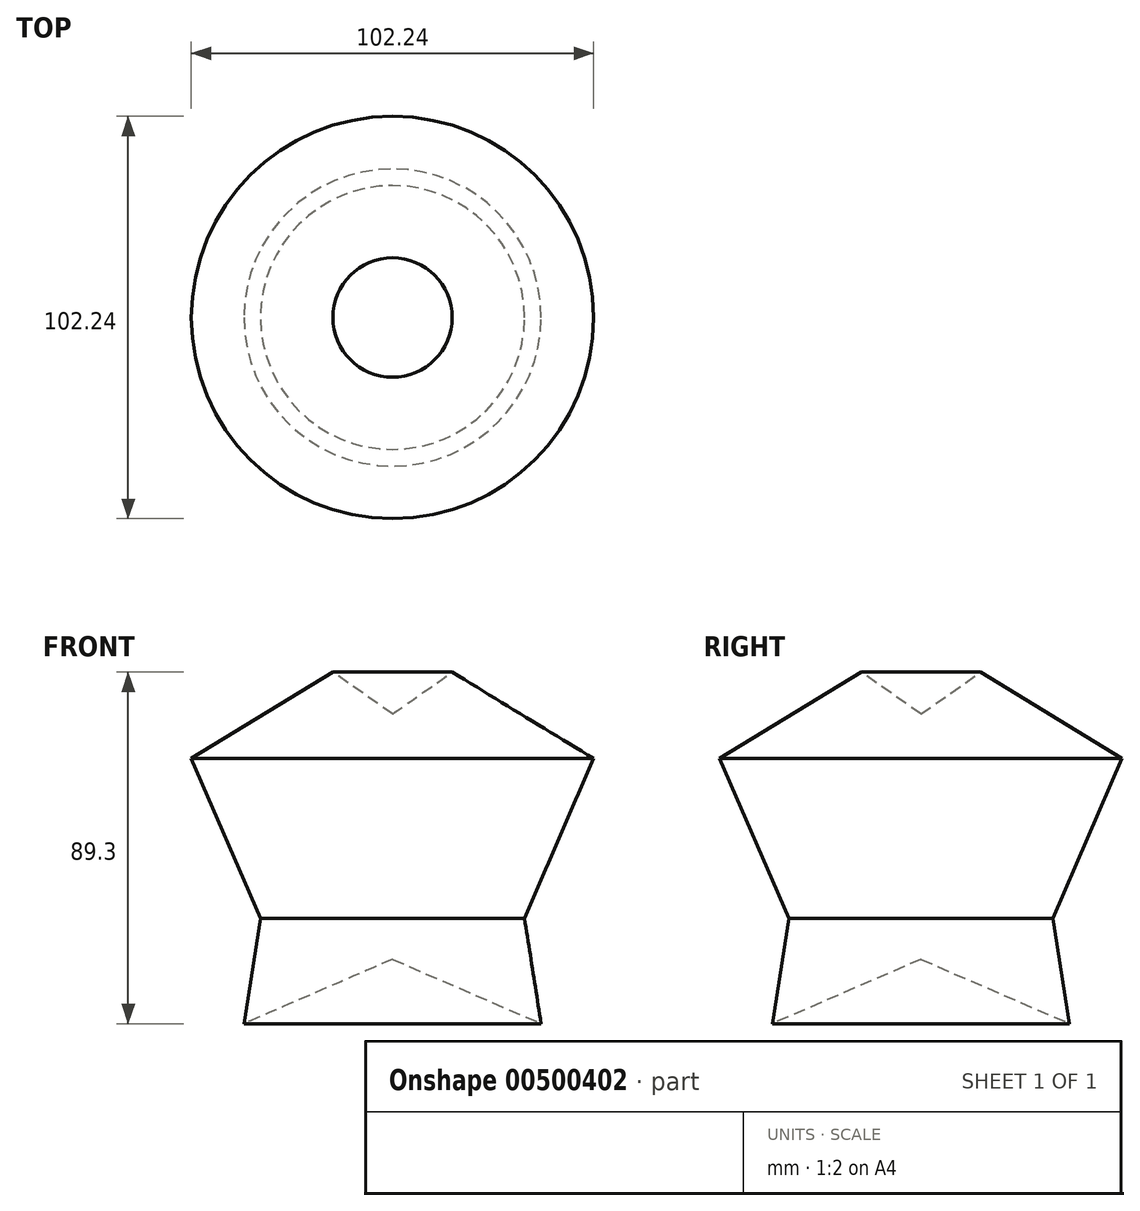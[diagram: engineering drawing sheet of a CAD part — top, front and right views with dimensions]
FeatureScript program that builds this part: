
annotation { "Feature Type Name" : "Feature", "Feature Type Description" : "" }
export const myFeature = defineFeature(function(context is Context, id is Id, definition is map)
    precondition{}
    {
        {
            var Q0;
            Q0=qCreatedBy(makeId("Front.planeOp"),FACE);
            var sketch = newSketch(context, id + "F0", { "sketchPlane" : qUnion([Q0])});
            skLineSegment(sketch, "E0", {"start": v(0, 0) * mm, "end": v(-58.03, 0) * mm});
            skLineSegment(sketch, "E1", {"start": v(-58.03, 0) * mm, "end": v(-19.1, 25.77) * mm});
            skLineSegment(sketch, "E2", {"start": v(-19.1, 25.77) * mm, "end": v(-44.29, 43.72) * mm});
            skLineSegment(sketch, "E3", {"start": v(-44.29, 43.72) * mm, "end": v(-19.1, 50.2) * mm});
            skLineSegment(sketch, "E4", {"start": v(-19.1, 50.2) * mm, "end": v(-22.23, 62.4) * mm});
            skLineSegment(sketch, "E5", {"start": v(-22.23, 62.4) * mm, "end": v(0, 62.4) * mm});
            skLineSegment(sketch, "E6", {"start": v(0, 62.4) * mm, "end": v(0, 0) * mm});
            skSolve(sketch);
        }
        {
            var Q0;
            Q0=qCreatedBy(makeId("Front.planeOp"),FACE);
            var sketch = newSketch(context, id + "F1", { "sketchPlane" : qUnion([Q0])});
            skLineSegment(sketch, "E7", {"start": v(-51.12, 24.78) * mm, "end": v(-33.53, -15.82) * mm});
            skLineSegment(sketch, "E8", {"start": v(-51.12, 24.78) * mm, "end": v(-15.17, 46.7) * mm});
            skLineSegment(sketch, "E9", {"start": v(-15.17, 46.7) * mm, "end": v(0, 36.08) * mm});
            skLineSegment(sketch, "E10", {"start": v(-37.75, -42.6) * mm, "end": v(0, -26.25) * mm});
            skLineSegment(sketch, "E11", {"start": v(-33.53, -15.82) * mm, "end": v(-37.75, -42.6) * mm});
            skPoint(sketch, "E12.orphan", {"position": v(-40.09, -57.46) * mm});
            skPoint(sketch, "E13.orphan", {"position": v(-40.09, -6.3) * mm});
            skLineSegment(sketch, "E14", {"start": v(0, 36.08) * mm, "end": v(0, -26.25) * mm});
            skSolve(sketch);
        }
        {
            var Q0;
            Q0 = qSketchRegion(id + "F1", true);
            var Q1;
            Q1=sQuery(id+"F1.wireOp",EDGE,"E14");
            revolve(context, id + "F2", {"entities" : qUnion([Q0]), "axis" : qUnion([Q1]), "revolveType" : RevolveType.FULL});
        }
    });
